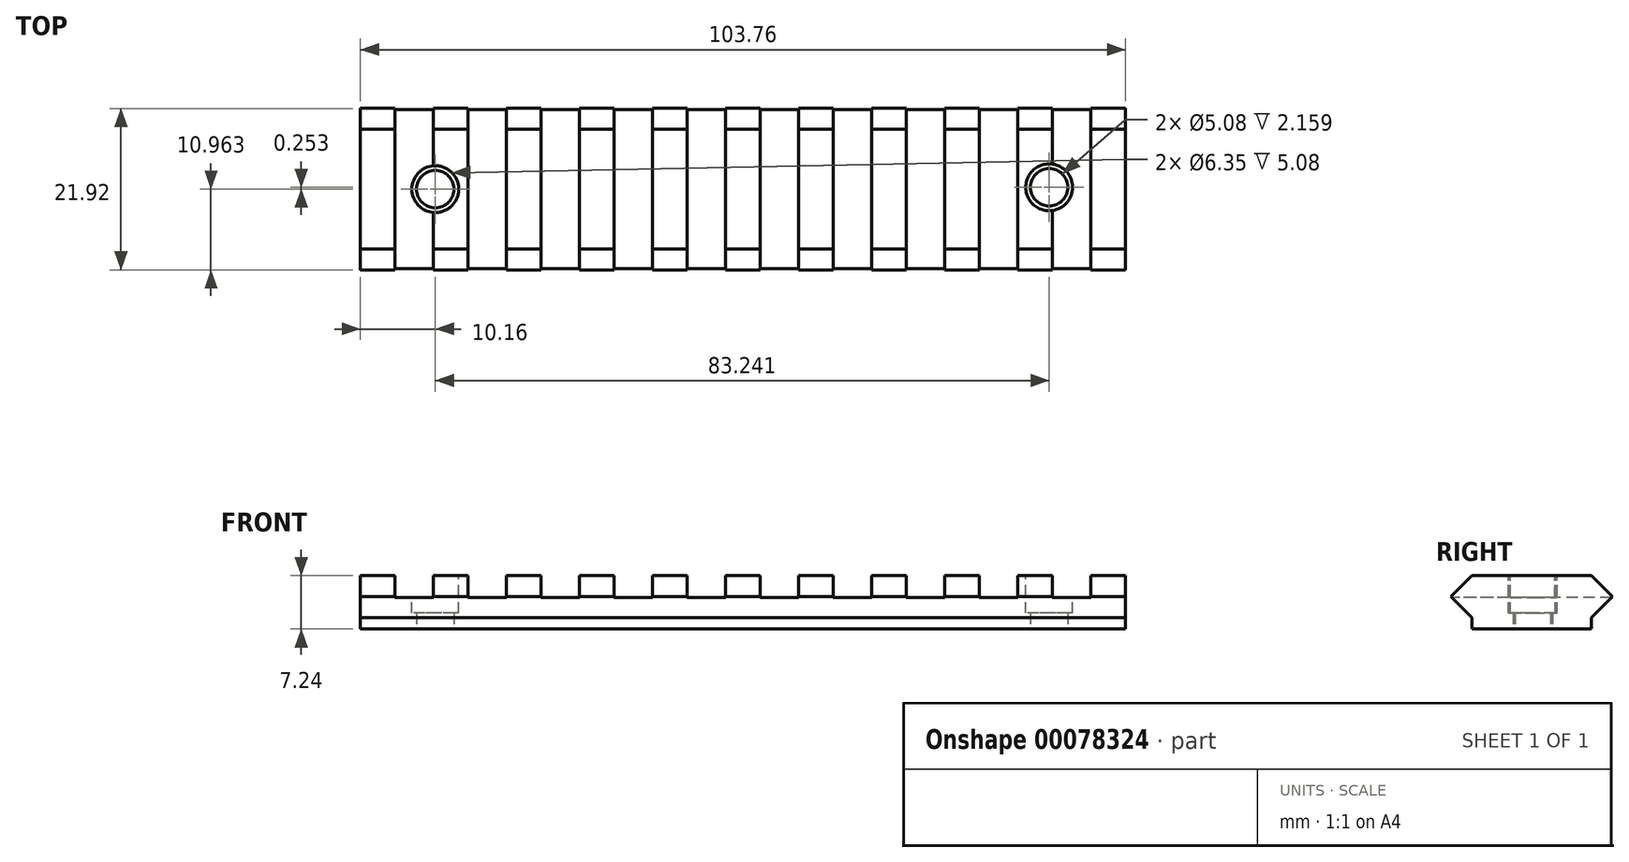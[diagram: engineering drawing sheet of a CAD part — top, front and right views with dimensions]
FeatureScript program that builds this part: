
annotation { "Feature Type Name" : "Feature", "Feature Type Description" : "" }
export const myFeature = defineFeature(function(context is Context, id is Id, definition is map)
    precondition{}
    {
        {
            var Q0;
            Q0=qCreatedBy(makeId("Right.planeOp"),FACE);
            var sketch = newSketch(context, id + "F0", { "sketchPlane" : qUnion([Q0])});
            skLineSegment(sketch, "E0", {"start": v(0, 0) * mm, "end": v(0, 1.52) * mm});
            skLineSegment(sketch, "E1", {"start": v(0, 1.52) * mm, "end": v(-2.86, 4.38) * mm});
            skLineSegment(sketch, "E2", {"start": v(-2.86, 4.38) * mm, "end": v(0, 7.24) * mm});
            skLineSegment(sketch, "E3", {"start": v(0, 7.24) * mm, "end": v(16.2, 7.24) * mm});
            skLineSegment(sketch, "E4", {"start": v(0, 0) * mm, "end": v(16.2, 0) * mm});
            skLineSegment(sketch, "E5", {"start": v(16.2, 0) * mm, "end": v(16.2, 1.52) * mm});
            skLineSegment(sketch, "E6", {"start": v(16.2, 1.52) * mm, "end": v(19.06, 4.38) * mm});
            skLineSegment(sketch, "E7", {"start": v(19.06, 4.38) * mm, "end": v(16.2, 7.24) * mm});
            skSolve(sketch);
        }
        {
            var Q0;
            Q0=makeQuery(id+"F0.imprint","IMPRINT",FACE,{"disambiguationData":[TD([[makeQuery(id+"F0.imprint","IMPRINT",EDGE,{"derivedFrom":sQuery(id+"F0.wireOp",EDGE,"E0")}),-1.0]])]});
            extrude(context, id + "F1", {"entities" : qUnion([Q0]), "depth" : 103.76 * mm});
        }
        {
            var Q0;
            Q0=makeQuery(id+"F1.opExtrude","SWEPT_FACE",FACE,{"disambiguationData":[OSD([sQuery(id+"F0.wireOp",EDGE,"E3")])]});
            var sketch = newSketch(context, id + "F2", { "sketchPlane" : qUnion([Q0])});
            skLineSegment(sketch, "E8", {"start": v(0, 8.1) * mm, "end": v(4.7, 8.1) * mm, "construction": true});
            skLineSegment(sketch, "E9", {"start": v(4.7, 8.1) * mm, "end": v(4.7, 19.06) * mm});
            skLineSegment(sketch, "E10", {"start": v(4.7, 8.1) * mm, "end": v(4.7, -2.86) * mm});
            skLineSegment(sketch, "E11", {"start": v(4.7, 8.1) * mm, "end": v(9.9, 8.1) * mm, "construction": true});
            skLineSegment(sketch, "E12", {"start": v(4.7, 19.06) * mm, "end": v(9.9, 19.06) * mm});
            skLineSegment(sketch, "E13", {"start": v(9.9, 19.06) * mm, "end": v(9.9, -2.86) * mm});
            skLineSegment(sketch, "E14", {"start": v(4.7, -2.86) * mm, "end": v(9.9, -2.86) * mm});
            skLineSegment(sketch, "E15", {"start": v(9.9, 8.1) * mm, "end": v(14.6, 8.1) * mm, "construction": true});
            skLineSegment(sketch, "E16.bottom", {"start": v(14.6, 19.06) * mm, "end": v(19.81, 19.06) * mm});
            skLineSegment(sketch, "E16.top", {"start": v(14.6, -2.86) * mm, "end": v(19.81, -2.86) * mm});
            skLineSegment(sketch, "E16.left", {"start": v(14.6, 19.06) * mm, "end": v(14.6, -2.86) * mm});
            skLineSegment(sketch, "E16.right", {"start": v(19.81, 19.06) * mm, "end": v(19.81, -2.86) * mm});
            skLineSegment(sketch, "E17", {"start": v(19.81, 8.1) * mm, "end": v(24.51, 8.1) * mm, "construction": true});
            skLineSegment(sketch, "E18.bottom", {"start": v(24.51, 19.06) * mm, "end": v(29.72, 19.06) * mm});
            skLineSegment(sketch, "E18.top", {"start": v(24.51, -2.86) * mm, "end": v(29.72, -2.86) * mm});
            skLineSegment(sketch, "E18.left", {"start": v(24.51, 19.06) * mm, "end": v(24.51, -2.86) * mm});
            skLineSegment(sketch, "E18.right", {"start": v(29.72, 19.06) * mm, "end": v(29.72, -2.86) * mm});
            skLineSegment(sketch, "E19.bottom", {"start": v(34.42, 19.06) * mm, "end": v(39.62, 19.06) * mm});
            skLineSegment(sketch, "E19.top", {"start": v(34.42, -2.86) * mm, "end": v(39.62, -2.86) * mm});
            skLineSegment(sketch, "E19.left", {"start": v(34.42, 19.06) * mm, "end": v(34.42, -2.86) * mm});
            skLineSegment(sketch, "E19.right", {"start": v(39.62, 19.06) * mm, "end": v(39.62, -2.86) * mm});
            skLineSegment(sketch, "E20", {"start": v(39.62, 8.1) * mm, "end": v(44.32, 8.1) * mm, "construction": true});
            skLineSegment(sketch, "E21.bottom", {"start": v(44.32, 19.06) * mm, "end": v(49.53, 19.06) * mm});
            skLineSegment(sketch, "E21.top", {"start": v(44.32, -2.86) * mm, "end": v(49.53, -2.86) * mm});
            skLineSegment(sketch, "E21.left", {"start": v(44.32, 19.06) * mm, "end": v(44.32, -2.86) * mm});
            skLineSegment(sketch, "E21.right", {"start": v(49.53, 19.06) * mm, "end": v(49.53, -2.86) * mm});
            skLineSegment(sketch, "E22", {"start": v(49.53, 8.1) * mm, "end": v(54.23, 8.1) * mm, "construction": true});
            skLineSegment(sketch, "E23.bottom", {"start": v(54.23, 19.06) * mm, "end": v(59.44, 19.06) * mm});
            skLineSegment(sketch, "E23.top", {"start": v(54.23, -2.86) * mm, "end": v(59.44, -2.86) * mm});
            skLineSegment(sketch, "E23.left", {"start": v(54.23, 19.06) * mm, "end": v(54.23, -2.86) * mm});
            skLineSegment(sketch, "E23.right", {"start": v(59.44, 19.06) * mm, "end": v(59.44, -2.86) * mm});
            skLineSegment(sketch, "E24", {"start": v(59.44, 8.1) * mm, "end": v(64.13, 8.1) * mm, "construction": true});
            skLineSegment(sketch, "E25.bottom", {"start": v(64.13, 19.06) * mm, "end": v(69.34, 19.06) * mm});
            skLineSegment(sketch, "E25.top", {"start": v(64.13, -2.86) * mm, "end": v(69.34, -2.86) * mm});
            skLineSegment(sketch, "E25.left", {"start": v(64.13, 19.06) * mm, "end": v(64.13, -2.86) * mm});
            skLineSegment(sketch, "E25.right", {"start": v(69.34, 19.06) * mm, "end": v(69.34, -2.86) * mm});
            skLineSegment(sketch, "E26", {"start": v(69.34, 8.1) * mm, "end": v(74.04, 8.1) * mm, "construction": true});
            skLineSegment(sketch, "E27", {"start": v(29.72, 8.1) * mm, "end": v(34.42, 8.1) * mm, "construction": true});
            skLineSegment(sketch, "E28.bottom", {"start": v(74.04, 19.06) * mm, "end": v(79.25, 19.06) * mm});
            skLineSegment(sketch, "E28.top", {"start": v(74.04, -2.86) * mm, "end": v(79.25, -2.86) * mm});
            skLineSegment(sketch, "E28.left", {"start": v(74.04, 19.06) * mm, "end": v(74.04, -2.86) * mm});
            skLineSegment(sketch, "E28.right", {"start": v(79.25, 19.06) * mm, "end": v(79.25, -2.86) * mm});
            skLineSegment(sketch, "E29", {"start": v(79.25, 8.1) * mm, "end": v(83.95, 8.1) * mm, "construction": true});
            skLineSegment(sketch, "E30.bottom", {"start": v(83.95, 19.06) * mm, "end": v(89.15, 19.06) * mm});
            skLineSegment(sketch, "E30.top", {"start": v(83.95, -2.86) * mm, "end": v(89.15, -2.86) * mm});
            skLineSegment(sketch, "E30.left", {"start": v(83.95, 19.06) * mm, "end": v(83.95, -2.86) * mm});
            skLineSegment(sketch, "E30.right", {"start": v(89.15, 19.06) * mm, "end": v(89.15, -2.86) * mm});
            skLineSegment(sketch, "E31", {"start": v(89.15, 8.1) * mm, "end": v(93.85, 8.1) * mm, "construction": true});
            skLineSegment(sketch, "E32.bottom", {"start": v(93.85, 19.15) * mm, "end": v(99.06, 19.15) * mm});
            skLineSegment(sketch, "E32.top", {"start": v(93.85, -2.94) * mm, "end": v(99.06, -2.94) * mm});
            skLineSegment(sketch, "E32.left", {"start": v(93.85, 19.15) * mm, "end": v(93.85, -2.94) * mm});
            skLineSegment(sketch, "E32.right", {"start": v(99.06, 19.15) * mm, "end": v(99.06, -2.94) * mm});
            skSolve(sketch);
        }
        {
            var Q0;
            {var subQ0=sQuery(id+"F2.wireOp",EDGE,"E14");Q0=makeQuery(id+"F2.imprint","IMPRINT",FACE,{"disambiguationData":[TD([[makeQuery(id+"F2.imprint","IMPRINT",EDGE,{"derivedFrom":subQ0}),1.0]])]});}
            var Q1;
            {var subQ0=sQuery(id+"F2.wireOp",EDGE,"E10");var subQ8=sQuery(id+"F2.wireOp",EDGE,"E9");var subQ9=makeQuery(id+"F2.imprint","INTERSECT",VERTEX,{"derivedFrom":[subQ8,subQ0]});Q1=makeQuery(id+"F2.imprint","IMPRINT",FACE,{"disambiguationData":[TD([[makeQuery(id+"F2.imprint","IMPRINT",EDGE,{"disambiguationData":[TD([[subQ9,-1.0]])],"derivedFrom":subQ8}),-1.0]])]});}
            var Q2;
            {var subQ0=sQuery(id+"F2.wireOp",EDGE,"E12");Q2=makeQuery(id+"F2.imprint","IMPRINT",FACE,{"disambiguationData":[TD([[makeQuery(id+"F2.imprint","IMPRINT",EDGE,{"derivedFrom":subQ0}),-1.0]])]});}
            var Q3;
            {var subQ0=sQuery(id+"F2.wireOp",EDGE,"E16.bottom");Q3=makeQuery(id+"F2.imprint","IMPRINT",FACE,{"disambiguationData":[TD([[makeQuery(id+"F2.imprint","IMPRINT",EDGE,{"derivedFrom":subQ0}),-1.0]])]});}
            var Q4;
            {var subQ0=sQuery(id+"F2.wireOp",EDGE,"E16.left");var subQ1=sQuery(id+"F0.wireOp",EDGE,"E3");var subQ2=makeQuery(id+"F1.opExtrude","SWEPT_EDGE",EDGE,{"disambiguationData":[OSD([subQ1,sQuery(id+"F0.wireOp",EDGE,"E7")])]});var subQ3=makeQuery(id+"F2.imprint","INTERSECT",VERTEX,{"derivedFrom":[subQ2,subQ0]});Q4=makeQuery(id+"F2.imprint","IMPRINT",FACE,{"disambiguationData":[TD([[makeQuery(id+"F2.imprint","IMPRINT",EDGE,{"disambiguationData":[TD([[subQ3,-1.0]])],"derivedFrom":subQ0}),1.0]])]});}
            var Q5;
            {var subQ0=sQuery(id+"F2.wireOp",EDGE,"E16.top");Q5=makeQuery(id+"F2.imprint","IMPRINT",FACE,{"disambiguationData":[TD([[makeQuery(id+"F2.imprint","IMPRINT",EDGE,{"derivedFrom":subQ0}),1.0]])]});}
            var Q6;
            {var subQ0=sQuery(id+"F2.wireOp",EDGE,"E18.bottom");Q6=makeQuery(id+"F2.imprint","IMPRINT",FACE,{"disambiguationData":[TD([[makeQuery(id+"F2.imprint","IMPRINT",EDGE,{"derivedFrom":subQ0}),-1.0]])]});}
            var Q7;
            {var subQ0=sQuery(id+"F2.wireOp",EDGE,"E18.left");var subQ1=sQuery(id+"F0.wireOp",EDGE,"E3");var subQ2=makeQuery(id+"F1.opExtrude","SWEPT_EDGE",EDGE,{"disambiguationData":[OSD([subQ1,sQuery(id+"F0.wireOp",EDGE,"E7")])]});var subQ3=makeQuery(id+"F2.imprint","INTERSECT",VERTEX,{"derivedFrom":[subQ2,subQ0]});Q7=makeQuery(id+"F2.imprint","IMPRINT",FACE,{"disambiguationData":[TD([[makeQuery(id+"F2.imprint","IMPRINT",EDGE,{"disambiguationData":[TD([[subQ3,-1.0]])],"derivedFrom":subQ0}),1.0]])]});}
            var Q8;
            {var subQ0=sQuery(id+"F2.wireOp",EDGE,"E18.top");Q8=makeQuery(id+"F2.imprint","IMPRINT",FACE,{"disambiguationData":[TD([[makeQuery(id+"F2.imprint","IMPRINT",EDGE,{"derivedFrom":subQ0}),1.0]])]});}
            var Q9;
            {var subQ0=sQuery(id+"F2.wireOp",EDGE,"E19.bottom");Q9=makeQuery(id+"F2.imprint","IMPRINT",FACE,{"disambiguationData":[TD([[makeQuery(id+"F2.imprint","IMPRINT",EDGE,{"derivedFrom":subQ0}),-1.0]])]});}
            var Q10;
            {var subQ0=sQuery(id+"F2.wireOp",EDGE,"E19.left");var subQ1=sQuery(id+"F0.wireOp",EDGE,"E3");var subQ2=makeQuery(id+"F1.opExtrude","SWEPT_EDGE",EDGE,{"disambiguationData":[OSD([subQ1,sQuery(id+"F0.wireOp",EDGE,"E7")])]});var subQ3=makeQuery(id+"F2.imprint","INTERSECT",VERTEX,{"derivedFrom":[subQ2,subQ0]});Q10=makeQuery(id+"F2.imprint","IMPRINT",FACE,{"disambiguationData":[TD([[makeQuery(id+"F2.imprint","IMPRINT",EDGE,{"disambiguationData":[TD([[subQ3,-1.0]])],"derivedFrom":subQ0}),1.0]])]});}
            var Q11;
            {var subQ0=sQuery(id+"F2.wireOp",EDGE,"E19.top");Q11=makeQuery(id+"F2.imprint","IMPRINT",FACE,{"disambiguationData":[TD([[makeQuery(id+"F2.imprint","IMPRINT",EDGE,{"derivedFrom":subQ0}),1.0]])]});}
            var Q12;
            {var subQ0=sQuery(id+"F2.wireOp",EDGE,"E21.bottom");Q12=makeQuery(id+"F2.imprint","IMPRINT",FACE,{"disambiguationData":[TD([[makeQuery(id+"F2.imprint","IMPRINT",EDGE,{"derivedFrom":subQ0}),-1.0]])]});}
            var Q13;
            {var subQ0=sQuery(id+"F2.wireOp",EDGE,"E21.left");var subQ1=sQuery(id+"F0.wireOp",EDGE,"E3");var subQ2=makeQuery(id+"F1.opExtrude","SWEPT_EDGE",EDGE,{"disambiguationData":[OSD([subQ1,sQuery(id+"F0.wireOp",EDGE,"E7")])]});var subQ3=makeQuery(id+"F2.imprint","INTERSECT",VERTEX,{"derivedFrom":[subQ2,subQ0]});Q13=makeQuery(id+"F2.imprint","IMPRINT",FACE,{"disambiguationData":[TD([[makeQuery(id+"F2.imprint","IMPRINT",EDGE,{"disambiguationData":[TD([[subQ3,-1.0]])],"derivedFrom":subQ0}),1.0]])]});}
            var Q14;
            {var subQ0=sQuery(id+"F2.wireOp",EDGE,"E21.top");Q14=makeQuery(id+"F2.imprint","IMPRINT",FACE,{"disambiguationData":[TD([[makeQuery(id+"F2.imprint","IMPRINT",EDGE,{"derivedFrom":subQ0}),1.0]])]});}
            var Q15;
            {var subQ0=sQuery(id+"F2.wireOp",EDGE,"E23.bottom");Q15=makeQuery(id+"F2.imprint","IMPRINT",FACE,{"disambiguationData":[TD([[makeQuery(id+"F2.imprint","IMPRINT",EDGE,{"derivedFrom":subQ0}),-1.0]])]});}
            var Q16;
            {var subQ0=sQuery(id+"F2.wireOp",EDGE,"E23.left");var subQ1=sQuery(id+"F0.wireOp",EDGE,"E3");var subQ2=makeQuery(id+"F1.opExtrude","SWEPT_EDGE",EDGE,{"disambiguationData":[OSD([subQ1,sQuery(id+"F0.wireOp",EDGE,"E7")])]});var subQ3=makeQuery(id+"F2.imprint","INTERSECT",VERTEX,{"derivedFrom":[subQ2,subQ0]});Q16=makeQuery(id+"F2.imprint","IMPRINT",FACE,{"disambiguationData":[TD([[makeQuery(id+"F2.imprint","IMPRINT",EDGE,{"disambiguationData":[TD([[subQ3,-1.0]])],"derivedFrom":subQ0}),1.0]])]});}
            var Q17;
            {var subQ0=sQuery(id+"F2.wireOp",EDGE,"E23.top");Q17=makeQuery(id+"F2.imprint","IMPRINT",FACE,{"disambiguationData":[TD([[makeQuery(id+"F2.imprint","IMPRINT",EDGE,{"derivedFrom":subQ0}),1.0]])]});}
            var Q18;
            {var subQ0=sQuery(id+"F2.wireOp",EDGE,"E25.bottom");Q18=makeQuery(id+"F2.imprint","IMPRINT",FACE,{"disambiguationData":[TD([[makeQuery(id+"F2.imprint","IMPRINT",EDGE,{"derivedFrom":subQ0}),-1.0]])]});}
            var Q19;
            {var subQ0=sQuery(id+"F2.wireOp",EDGE,"E25.left");var subQ1=sQuery(id+"F0.wireOp",EDGE,"E3");var subQ2=makeQuery(id+"F1.opExtrude","SWEPT_EDGE",EDGE,{"disambiguationData":[OSD([subQ1,sQuery(id+"F0.wireOp",EDGE,"E7")])]});var subQ3=makeQuery(id+"F2.imprint","INTERSECT",VERTEX,{"derivedFrom":[subQ2,subQ0]});Q19=makeQuery(id+"F2.imprint","IMPRINT",FACE,{"disambiguationData":[TD([[makeQuery(id+"F2.imprint","IMPRINT",EDGE,{"disambiguationData":[TD([[subQ3,-1.0]])],"derivedFrom":subQ0}),1.0]])]});}
            var Q20;
            {var subQ0=sQuery(id+"F2.wireOp",EDGE,"E25.top");Q20=makeQuery(id+"F2.imprint","IMPRINT",FACE,{"disambiguationData":[TD([[makeQuery(id+"F2.imprint","IMPRINT",EDGE,{"derivedFrom":subQ0}),1.0]])]});}
            var Q21;
            {var subQ0=sQuery(id+"F2.wireOp",EDGE,"E28.bottom");Q21=makeQuery(id+"F2.imprint","IMPRINT",FACE,{"disambiguationData":[TD([[makeQuery(id+"F2.imprint","IMPRINT",EDGE,{"derivedFrom":subQ0}),-1.0]])]});}
            var Q22;
            {var subQ0=sQuery(id+"F2.wireOp",EDGE,"E28.left");var subQ1=sQuery(id+"F0.wireOp",EDGE,"E3");var subQ2=makeQuery(id+"F1.opExtrude","SWEPT_EDGE",EDGE,{"disambiguationData":[OSD([subQ1,sQuery(id+"F0.wireOp",EDGE,"E7")])]});var subQ3=makeQuery(id+"F2.imprint","INTERSECT",VERTEX,{"derivedFrom":[subQ2,subQ0]});Q22=makeQuery(id+"F2.imprint","IMPRINT",FACE,{"disambiguationData":[TD([[makeQuery(id+"F2.imprint","IMPRINT",EDGE,{"disambiguationData":[TD([[subQ3,-1.0]])],"derivedFrom":subQ0}),1.0]])]});}
            var Q23;
            {var subQ0=sQuery(id+"F2.wireOp",EDGE,"E28.top");Q23=makeQuery(id+"F2.imprint","IMPRINT",FACE,{"disambiguationData":[TD([[makeQuery(id+"F2.imprint","IMPRINT",EDGE,{"derivedFrom":subQ0}),1.0]])]});}
            var Q24;
            {var subQ0=sQuery(id+"F2.wireOp",EDGE,"E30.top");Q24=makeQuery(id+"F2.imprint","IMPRINT",FACE,{"disambiguationData":[TD([[makeQuery(id+"F2.imprint","IMPRINT",EDGE,{"derivedFrom":subQ0}),1.0]])]});}
            var Q25;
            {var subQ0=sQuery(id+"F2.wireOp",EDGE,"E30.left");var subQ1=sQuery(id+"F0.wireOp",EDGE,"E3");var subQ2=makeQuery(id+"F1.opExtrude","SWEPT_EDGE",EDGE,{"disambiguationData":[OSD([subQ1,sQuery(id+"F0.wireOp",EDGE,"E7")])]});var subQ3=makeQuery(id+"F2.imprint","INTERSECT",VERTEX,{"derivedFrom":[subQ2,subQ0]});Q25=makeQuery(id+"F2.imprint","IMPRINT",FACE,{"disambiguationData":[TD([[makeQuery(id+"F2.imprint","IMPRINT",EDGE,{"disambiguationData":[TD([[subQ3,-1.0]])],"derivedFrom":subQ0}),1.0]])]});}
            var Q26;
            {var subQ0=sQuery(id+"F2.wireOp",EDGE,"E30.bottom");Q26=makeQuery(id+"F2.imprint","IMPRINT",FACE,{"disambiguationData":[TD([[makeQuery(id+"F2.imprint","IMPRINT",EDGE,{"derivedFrom":subQ0}),-1.0]])]});}
            var Q27;
            {var subQ0=sQuery(id+"F2.wireOp",EDGE,"E32.bottom");Q27=makeQuery(id+"F2.imprint","IMPRINT",FACE,{"disambiguationData":[TD([[makeQuery(id+"F2.imprint","IMPRINT",EDGE,{"derivedFrom":subQ0}),-1.0]])]});}
            var Q28;
            {var subQ0=sQuery(id+"F2.wireOp",EDGE,"E32.left");var subQ1=sQuery(id+"F0.wireOp",EDGE,"E3");var subQ2=makeQuery(id+"F1.opExtrude","SWEPT_EDGE",EDGE,{"disambiguationData":[OSD([subQ1,sQuery(id+"F0.wireOp",EDGE,"E7")])]});var subQ3=makeQuery(id+"F2.imprint","INTERSECT",VERTEX,{"derivedFrom":[subQ2,subQ0]});Q28=makeQuery(id+"F2.imprint","IMPRINT",FACE,{"disambiguationData":[TD([[makeQuery(id+"F2.imprint","IMPRINT",EDGE,{"disambiguationData":[TD([[subQ3,-1.0]])],"derivedFrom":subQ0}),1.0]])]});}
            var Q29;
            {var subQ0=sQuery(id+"F2.wireOp",EDGE,"E32.top");Q29=makeQuery(id+"F2.imprint","IMPRINT",FACE,{"disambiguationData":[TD([[makeQuery(id+"F2.imprint","IMPRINT",EDGE,{"derivedFrom":subQ0}),1.0]])]});}
            extrude(context, id + "F3", {"entities" : qUnion([Q0, Q1, Q2, Q3, Q4, Q5, Q6, Q7, Q8, Q9, Q10, Q11, Q12, Q13, Q14, Q15, Q16, Q17, Q18, Q19, Q20, Q21, Q22, Q23, Q24, Q25, Q26, Q27, Q28, Q29]), "operationType" : NewBodyOperationType.REMOVE, "oppositeDirection" : true, "depth" : 3 * mm});
        }
        {
            var Q0;
            Q0=makeQuery(id+"F1.opExtrude","SWEPT_FACE",FACE,{"disambiguationData":[OSD([sQuery(id+"F0.wireOp",EDGE,"E4")])]});
            var sketch = newSketch(context, id + "F4", { "sketchPlane" : qUnion([Q0])});
            skCircle(sketch, "E33", {"center": v(93.4, -8.36) * mm, "radius": 2.54 * mm});
            skCircle(sketch, "E34", {"center": v(10.16, -8.1) * mm, "radius": 2.54 * mm});
            skLineSegment(sketch, "E35", {"start": v(10.16, -8.1) * mm, "end": v(0, -8.1) * mm, "construction": true});
            skPoint(sketch, "E35.endSnap0", {"position": v(0, -8.1) * mm});
            skLineSegment(sketch, "E36", {"start": v(93.4, -8.36) * mm, "end": v(10.16, -8.1) * mm, "construction": true});
            skSolve(sketch);
        }
        {
            var Q0;
            Q0=makeQuery(id+"F4.imprint","IMPRINT",FACE,{"disambiguationData":[TD([[makeQuery(id+"F4.imprint","IMPRINT",EDGE,{"derivedFrom":sQuery(id+"F4.wireOp",EDGE,"E33")}),1.0]])]});
            var Q1;
            Q1=makeQuery(id+"F4.imprint","IMPRINT",FACE,{"disambiguationData":[TD([[makeQuery(id+"F4.imprint","IMPRINT",EDGE,{"derivedFrom":sQuery(id+"F4.wireOp",EDGE,"E34")}),1.0]])]});
            extrude(context, id + "F5", {"entities" : qUnion([Q0, Q1]), "operationType" : NewBodyOperationType.REMOVE, "oppositeDirection" : true, "depth" : 7.24 * mm});
        }
        {
            var Q0;
            Q0=makeQuery(id+"F3.boolean.opBoolean","SPLIT",FACE,{"disambiguationData":[TD([makeQuery(id+"F3.opExtrude","SWEPT_FACE",FACE,{"disambiguationData":[OSD([sQuery(id+"F2.wireOp",EDGE,"E18.right")])]})])],"derivedFrom":makeQuery(id+"F1.opExtrude","SWEPT_FACE",FACE,{"disambiguationData":[OSD([sQuery(id+"F0.wireOp",EDGE,"E3")])]})});
            var sketch = newSketch(context, id + "F6", { "sketchPlane" : qUnion([Q0])});
            skCircle(sketch, "E37", {"center": v(10.16, 8.1) * mm, "radius": 3.18 * mm});
            skCircle(sketch, "E38", {"center": v(93.4, 8.36) * mm, "radius": 3.18 * mm});
            skCircle(sketch, "E39", {"center": v(10.16, 8.1) * mm, "radius": 2.54 * mm, "construction": true});
            skCircle(sketch, "E40", {"center": v(93.4, 8.36) * mm, "radius": 2.54 * mm, "construction": true});
            skSolve(sketch);
        }
        {
            var Q0;
            Q0=makeQuery(id+"F6.imprint","IMPRINT",FACE,{"disambiguationData":[TD([[makeQuery(id+"F6.imprint","IMPRINT",EDGE,{"derivedFrom":sQuery(id+"F6.wireOp",EDGE,"E38")}),1.0]])]});
            var Q1;
            Q1=makeQuery(id+"F6.imprint","IMPRINT",FACE,{"disambiguationData":[TD([[makeQuery(id+"F6.imprint","IMPRINT",EDGE,{"derivedFrom":sQuery(id+"F6.wireOp",EDGE,"E37")}),1.0]])]});
            extrude(context, id + "F7", {"entities" : qUnion([Q0, Q1]), "operationType" : NewBodyOperationType.REMOVE, "oppositeDirection" : true, "depth" : 5.08 * mm});
        }
    });
